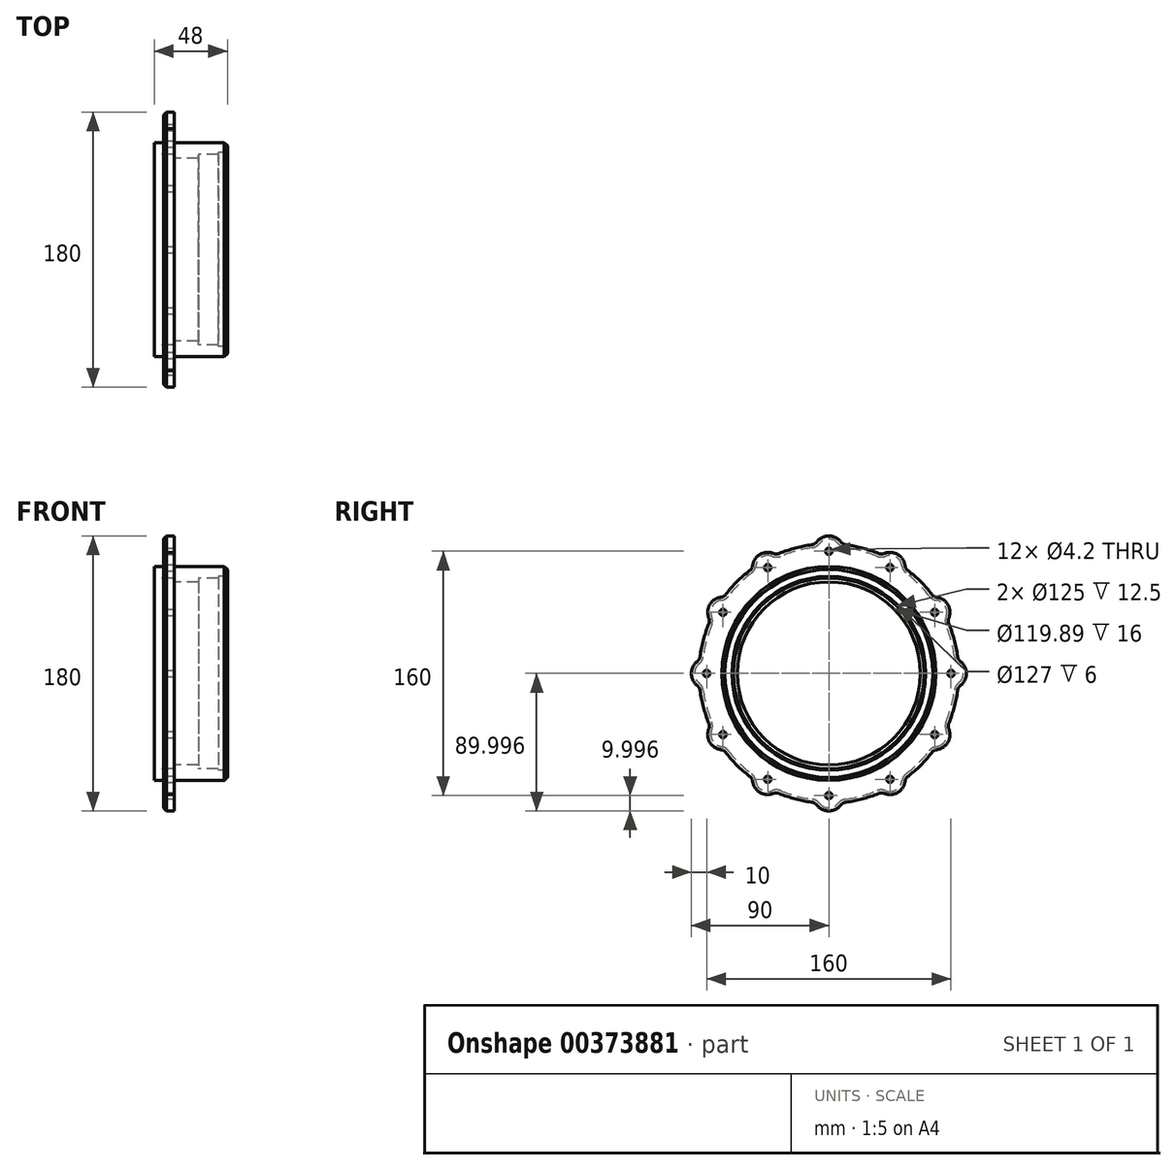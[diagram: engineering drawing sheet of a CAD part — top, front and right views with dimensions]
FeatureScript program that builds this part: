
annotation { "Feature Type Name" : "Feature", "Feature Type Description" : "" }
export const myFeature = defineFeature(function(context is Context, id is Id, definition is map)
    precondition{}
    {
        {
            var Q0;
            Q0=qCreatedBy(makeId("Front.planeOp"),FACE);
            var sketch = newSketch(context, id + "F0", { "sketchPlane" : qUnion([Q0])});
            skLineSegment(sketch, "E0", {"start": v(-16.87, 26.2) * mm, "end": v(-9.87, 26.2) * mm});
            skLineSegment(sketch, "E1", {"start": v(-9.87, 26.2) * mm, "end": v(-9.87, 6.2) * mm});
            skLineSegment(sketch, "E2", {"start": v(-16.87, 26.2) * mm, "end": v(-16.87, 6.2) * mm});
            skLineSegment(sketch, "E3", {"start": v(-16.87, 6.2) * mm, "end": v(-22.87, 6.2) * mm});
            skLineSegment(sketch, "E4", {"start": v(-22.87, 6.2) * mm, "end": v(-22.87, -1.3) * mm});
            skLineSegment(sketch, "E5", {"start": v(-22.87, -1.3) * mm, "end": v(-9.87, -1.3) * mm});
            skLineSegment(sketch, "E6", {"start": v(-9.87, -1.3) * mm, "end": v(-9.87, -3.85) * mm});
            skLineSegment(sketch, "E7", {"start": v(-9.87, -3.85) * mm, "end": v(6.13, -3.85) * mm});
            skLineSegment(sketch, "E8", {"start": v(6.13, -3.85) * mm, "end": v(6.13, -1.3) * mm});
            skLineSegment(sketch, "E9", {"start": v(6.13, -1.3) * mm, "end": v(19.13, -1.3) * mm});
            skLineSegment(sketch, "E10", {"start": v(-16.87, -63.8) * mm, "end": v(53.32, -63.8) * mm, "construction": true});
            skLineSegment(sketch, "E11", {"start": v(19.13, -1.3) * mm, "end": v(19.13, -0.3) * mm});
            skLineSegment(sketch, "E12", {"start": v(19.13, -0.3) * mm, "end": v(25.13, -0.3) * mm});
            skLineSegment(sketch, "E13", {"start": v(-9.87, 6.2) * mm, "end": v(25.13, 6.2) * mm});
            skLineSegment(sketch, "E14", {"start": v(25.13, 6.2) * mm, "end": v(25.13, -0.3) * mm});
            skSolve(sketch);
        }
        {
            var Q0;
            Q0 = qSketchRegion(id + "F0", true);
            var Q1;
            Q1=sQuery(id+"F0.wireOp",EDGE,"E10");
            revolve(context, id + "F1", {"entities" : qUnion([Q0]), "axis" : qUnion([Q1]), "revolveType" : RevolveType.FULL});
        }
        {
            var Q0;
            Q0=makeQuery(id+"F1.opRevolve","SWEPT_FACE",FACE,{"disambiguationData":[OSD([sQuery(id+"F0.wireOp",EDGE,"E2")])]});
            var sketch = newSketch(context, id + "F2", { "sketchPlane" : qUnion([Q0])});
            skLineSegment(sketch, "E15", {"start": v(0, -63.8) * mm, "end": v(0, 16.2) * mm, "construction": true});
            skPoint(sketch, "E16", {"position": v(0, 16.2) * mm});
            skPoint(sketch, "E17.1.0", {"position": v(-40, 5.49) * mm});
            skPoint(sketch, "E17.2.0", {"position": v(-69.28, -23.8) * mm});
            skPoint(sketch, "E17.3.0", {"position": v(-80, -63.8) * mm});
            skPoint(sketch, "E17.4.0", {"position": v(-69.28, -103.8) * mm});
            skPoint(sketch, "E17.5.0", {"position": v(-40, -133.08) * mm});
            skPoint(sketch, "E17.6.0", {"position": v(0, -143.8) * mm});
            skPoint(sketch, "E17.7.0", {"position": v(40, -133.08) * mm});
            skPoint(sketch, "E17.8.0", {"position": v(69.28, -103.8) * mm});
            skPoint(sketch, "E17.9.0", {"position": v(80, -63.8) * mm});
            skPoint(sketch, "E17.10.0", {"position": v(69.28, -23.8) * mm});
            skPoint(sketch, "E17.11.0", {"position": v(40, 5.49) * mm});
            skPoint(sketch, "E17.center", {"position": v(0, -63.8) * mm});
            skSolve(sketch);
        }
        {
            var Q0;
            Q0=sQuery(id+"F2.wireOp",VERTEX,"E16");
            var Q1;
            Q1=sQuery(id+"F2.wireOp",VERTEX,"E17.11.0");
            var Q2;
            Q2=sQuery(id+"F2.wireOp",VERTEX,"E17.10.0");
            var Q3;
            Q3=sQuery(id+"F2.wireOp",VERTEX,"E17.9.0");
            var Q4;
            Q4=sQuery(id+"F2.wireOp",VERTEX,"E17.8.0");
            var Q5;
            Q5=sQuery(id+"F2.wireOp",VERTEX,"E17.7.0");
            var Q6;
            Q6=sQuery(id+"F2.wireOp",VERTEX,"E17.6.0");
            var Q7;
            Q7=sQuery(id+"F2.wireOp",VERTEX,"E17.5.0");
            var Q8;
            Q8=sQuery(id+"F2.wireOp",VERTEX,"E17.4.0");
            var Q9;
            Q9=sQuery(id+"F2.wireOp",VERTEX,"E17.3.0");
            var Q10;
            Q10=sQuery(id+"F2.wireOp",VERTEX,"E17.2.0");
            var Q11;
            Q11=sQuery(id+"F2.wireOp",VERTEX,"E17.1.0");
            var Q12;
            Q12=makeQuery(id+"F1.opRevolve","SWEPT_BODY",BODY,{"disambiguationData":[OSD([sQuery(id+"F0.wireOp",EDGE,"E0"),sQuery(id+"F0.wireOp",EDGE,"E1"),sQuery(id+"F0.wireOp",EDGE,"E2"),sQuery(id+"F0.wireOp",EDGE,"E3"),sQuery(id+"F0.wireOp",EDGE,"E4"),sQuery(id+"F0.wireOp",EDGE,"E5"),sQuery(id+"F0.wireOp",EDGE,"E6"),sQuery(id+"F0.wireOp",EDGE,"E7"),sQuery(id+"F0.wireOp",EDGE,"E8"),sQuery(id+"F0.wireOp",EDGE,"E9"),sQuery(id+"F0.wireOp",EDGE,"E11"),sQuery(id+"F0.wireOp",EDGE,"E12"),sQuery(id+"F0.wireOp",EDGE,"E13"),sQuery(id+"F0.wireOp",EDGE,"E14")])]});
            hole(context, id + "F3", {"style" : HoleStyle.SIMPLE, "endStyle" : HoleEndStyle.THROUGH, "standardTappedOrClearance" : lookupTablePath({ "standard" : "ISO", "engagement" : "75%", "pitch" : "0.8 mm", "size" : "M5", "type" : "Tapped" }), "standardBlindInLast" : lookupTablePath({ "standard" : "ISO", "engagement" : "75%", "pitch" : "0.8 mm", "size" : "M5", "type" : "Tapped" }), "holeDiameter" : 4.2 * mm, "showTappedDepth" : true, "isTappedThrough" : true, "tappedDepth" : 16.82 * mm, "tapClearance" : 3, "locations" : qUnion([Q0, Q1, Q2, Q3, Q4, Q5, Q6, Q7, Q8, Q9, Q10, Q11]), "scope" : qUnion([Q12]), "majorDiameter" : 5 * mm, "startStyle" : HoleStartStyle.SKETCH});
        }
        {
            var Q0;
            Q0=makeQuery(id+"F1.opRevolve","SWEPT_FACE",FACE,{"disambiguationData":[OSD([sQuery(id+"F0.wireOp",EDGE,"E1")])]});
            var sketch = newSketch(context, id + "F4", { "sketchPlane" : qUnion([Q0])});
            skArc(sketch, "E18", {"start": v(45, 14.15) * mm, "mid": v(40.7, 15.46) * mm, "end": v(36.24, 14.75) * mm});
            skArc(sketch, "E19", {"start": v(7.89, 22.35) * mm, "mid": v(4.39, 25.2) * mm, "end": v(0, 26.2) * mm});
            skArc(sketch, "E20", {"start": v(32.45, 14.77) * mm, "mid": v(22, 18.3) * mm, "end": v(11.18, 20.47) * mm});
            skLineSegment(sketch, "E21", {"start": v(0, -63.8) * mm, "end": v(0, 34.34) * mm, "construction": true});
            skLineSegment(sketch, "E22", {"start": v(0, -63.8) * mm, "end": v(49.04, 21.14) * mm, "construction": true});
            skPoint(sketch, "E23.visualSharp", {"position": v(8.91, 20.74) * mm});
            skArc(sketch, "E23.filletArc", {"start": v(7.89, 22.35) * mm, "mid": v(9.35, 21.09) * mm, "end": v(11.18, 20.47) * mm});
            skPoint(sketch, "E24.visualSharp", {"position": v(34.55, 13.87) * mm});
            skArc(sketch, "E24.filletArc", {"start": v(32.45, 14.77) * mm, "mid": v(34.35, 14.39) * mm, "end": v(36.24, 14.75) * mm});
            skPoint(sketch, "E25.1.0", {"position": v(-34.55, 13.87) * mm});
            skArc(sketch, "E25.1.1", {"start": v(-11.18, 20.47) * mm, "mid": v(-22, 18.3) * mm, "end": v(-32.45, 14.77) * mm});
            skArc(sketch, "E25.1.2", {"start": v(-36.24, 14.75) * mm, "mid": v(-40.7, 15.46) * mm, "end": v(-45, 14.15) * mm});
            skPoint(sketch, "E25.1.3", {"position": v(-8.91, 20.74) * mm});
            skArc(sketch, "E25.1.4", {"start": v(0, 26.2) * mm, "mid": v(-4.39, 25.2) * mm, "end": v(-7.89, 22.35) * mm});
            skArc(sketch, "E25.1.5", {"start": v(-11.18, 20.47) * mm, "mid": v(-9.35, 21.09) * mm, "end": v(-7.89, 22.35) * mm});
            skArc(sketch, "E25.1.6", {"start": v(-36.24, 14.75) * mm, "mid": v(-34.35, 14.39) * mm, "end": v(-32.45, 14.77) * mm});
            skPoint(sketch, "E25.2.0", {"position": v(-68.75, -13.8) * mm});
            skArc(sketch, "E25.2.1", {"start": v(-51.8, 3.6) * mm, "mid": v(-60.1, -3.7) * mm, "end": v(-67.39, -11.98) * mm});
            skArc(sketch, "E25.2.2", {"start": v(-70.66, -13.89) * mm, "mid": v(-74.87, -15.5) * mm, "end": v(-77.94, -18.8) * mm});
            skPoint(sketch, "E25.2.3", {"position": v(-49.99, 4.95) * mm});
            skArc(sketch, "E25.2.4", {"start": v(-45, 14.15) * mm, "mid": v(-48.3, 11.07) * mm, "end": v(-49.9, 6.87) * mm});
            skArc(sketch, "E25.2.5", {"start": v(-51.8, 3.6) * mm, "mid": v(-50.53, 5.04) * mm, "end": v(-49.9, 6.87) * mm});
            skArc(sketch, "E25.2.6", {"start": v(-70.66, -13.89) * mm, "mid": v(-68.84, -13.26) * mm, "end": v(-67.39, -11.98) * mm});
            skPoint(sketch, "E25.3.0", {"position": v(-84.53, -54.88) * mm});
            skArc(sketch, "E25.3.1", {"start": v(-78.56, -31.34) * mm, "mid": v(-82.1, -41.8) * mm, "end": v(-84.26, -52.62) * mm});
            skArc(sketch, "E25.3.2", {"start": v(-86.15, -55.9) * mm, "mid": v(-88.98, -59.4) * mm, "end": v(-90, -63.8) * mm});
            skPoint(sketch, "E25.3.3", {"position": v(-77.66, -29.25) * mm});
            skArc(sketch, "E25.3.4", {"start": v(-77.94, -18.8) * mm, "mid": v(-79.26, -23.1) * mm, "end": v(-78.55, -27.55) * mm});
            skArc(sketch, "E25.3.5", {"start": v(-78.56, -31.34) * mm, "mid": v(-78.18, -29.45) * mm, "end": v(-78.55, -27.55) * mm});
            skArc(sketch, "E25.3.6", {"start": v(-86.15, -55.9) * mm, "mid": v(-84.88, -54.45) * mm, "end": v(-84.26, -52.62) * mm});
            skPoint(sketch, "E25.4.0", {"position": v(-77.66, -98.34) * mm});
            skArc(sketch, "E25.4.1", {"start": v(-84.26, -74.97) * mm, "mid": v(-82.1, -85.8) * mm, "end": v(-78.56, -96.25) * mm});
            skArc(sketch, "E25.4.2", {"start": v(-78.55, -100.04) * mm, "mid": v(-79.26, -104.48) * mm, "end": v(-77.94, -108.8) * mm});
            skPoint(sketch, "E25.4.3", {"position": v(-84.53, -72.7) * mm});
            skArc(sketch, "E25.4.4", {"start": v(-90, -63.8) * mm, "mid": v(-88.98, -68.18) * mm, "end": v(-86.15, -71.68) * mm});
            skArc(sketch, "E25.4.5", {"start": v(-84.26, -74.97) * mm, "mid": v(-84.88, -73.14) * mm, "end": v(-86.15, -71.68) * mm});
            skArc(sketch, "E25.4.6", {"start": v(-78.55, -100.04) * mm, "mid": v(-78.18, -98.14) * mm, "end": v(-78.56, -96.25) * mm});
            skPoint(sketch, "E25.5.0", {"position": v(-49.99, -132.54) * mm});
            skArc(sketch, "E25.5.1", {"start": v(-67.39, -115.6) * mm, "mid": v(-60.1, -123.9) * mm, "end": v(-51.8, -131.18) * mm});
            skArc(sketch, "E25.5.2", {"start": v(-49.9, -134.45) * mm, "mid": v(-48.3, -138.66) * mm, "end": v(-45, -141.74) * mm});
            skPoint(sketch, "E25.5.3", {"position": v(-68.75, -113.78) * mm});
            skArc(sketch, "E25.5.4", {"start": v(-77.94, -108.8) * mm, "mid": v(-74.87, -112.09) * mm, "end": v(-70.66, -113.7) * mm});
            skArc(sketch, "E25.5.5", {"start": v(-67.39, -115.6) * mm, "mid": v(-68.84, -114.33) * mm, "end": v(-70.66, -113.7) * mm});
            skArc(sketch, "E25.5.6", {"start": v(-49.9, -134.45) * mm, "mid": v(-50.53, -132.63) * mm, "end": v(-51.8, -131.18) * mm});
            skPoint(sketch, "E25.6.0", {"position": v(-8.91, -148.33) * mm});
            skArc(sketch, "E25.6.1", {"start": v(-32.45, -142.36) * mm, "mid": v(-22, -145.9) * mm, "end": v(-11.18, -148.06) * mm});
            skArc(sketch, "E25.6.2", {"start": v(-7.89, -149.94) * mm, "mid": v(-4.39, -152.78) * mm, "end": v(0, -153.8) * mm});
            skPoint(sketch, "E25.6.3", {"position": v(-34.55, -141.46) * mm});
            skArc(sketch, "E25.6.4", {"start": v(-45, -141.74) * mm, "mid": v(-40.7, -143.05) * mm, "end": v(-36.24, -142.34) * mm});
            skArc(sketch, "E25.6.5", {"start": v(-32.45, -142.36) * mm, "mid": v(-34.35, -141.98) * mm, "end": v(-36.24, -142.34) * mm});
            skArc(sketch, "E25.6.6", {"start": v(-7.89, -149.94) * mm, "mid": v(-9.35, -148.67) * mm, "end": v(-11.18, -148.06) * mm});
            skPoint(sketch, "E25.7.0", {"position": v(34.55, -141.46) * mm});
            skArc(sketch, "E25.7.1", {"start": v(11.18, -148.06) * mm, "mid": v(22, -145.9) * mm, "end": v(32.45, -142.36) * mm});
            skArc(sketch, "E25.7.2", {"start": v(36.24, -142.34) * mm, "mid": v(40.7, -143.05) * mm, "end": v(45, -141.74) * mm});
            skPoint(sketch, "E25.7.3", {"position": v(8.91, -148.33) * mm});
            skArc(sketch, "E25.7.4", {"start": v(0, -153.8) * mm, "mid": v(4.39, -152.78) * mm, "end": v(7.89, -149.94) * mm});
            skArc(sketch, "E25.7.5", {"start": v(11.18, -148.06) * mm, "mid": v(9.35, -148.67) * mm, "end": v(7.89, -149.94) * mm});
            skArc(sketch, "E25.7.6", {"start": v(36.24, -142.34) * mm, "mid": v(34.35, -141.98) * mm, "end": v(32.45, -142.36) * mm});
            skPoint(sketch, "E25.8.0", {"position": v(68.75, -113.78) * mm});
            skArc(sketch, "E25.8.1", {"start": v(51.8, -131.18) * mm, "mid": v(60.1, -123.9) * mm, "end": v(67.39, -115.6) * mm});
            skArc(sketch, "E25.8.2", {"start": v(70.66, -113.7) * mm, "mid": v(74.87, -112.09) * mm, "end": v(77.94, -108.8) * mm});
            skPoint(sketch, "E25.8.3", {"position": v(49.99, -132.54) * mm});
            skArc(sketch, "E25.8.4", {"start": v(45, -141.74) * mm, "mid": v(48.3, -138.66) * mm, "end": v(49.9, -134.45) * mm});
            skArc(sketch, "E25.8.5", {"start": v(51.8, -131.18) * mm, "mid": v(50.53, -132.63) * mm, "end": v(49.9, -134.45) * mm});
            skArc(sketch, "E25.8.6", {"start": v(70.66, -113.7) * mm, "mid": v(68.84, -114.33) * mm, "end": v(67.39, -115.6) * mm});
            skPoint(sketch, "E25.9.0", {"position": v(84.53, -72.7) * mm});
            skArc(sketch, "E25.9.1", {"start": v(78.56, -96.25) * mm, "mid": v(82.1, -85.8) * mm, "end": v(84.26, -74.97) * mm});
            skArc(sketch, "E25.9.2", {"start": v(86.15, -71.68) * mm, "mid": v(88.98, -68.18) * mm, "end": v(90, -63.8) * mm});
            skPoint(sketch, "E25.9.3", {"position": v(77.66, -98.34) * mm});
            skArc(sketch, "E25.9.4", {"start": v(77.94, -108.8) * mm, "mid": v(79.26, -104.48) * mm, "end": v(78.55, -100.04) * mm});
            skArc(sketch, "E25.9.5", {"start": v(78.56, -96.25) * mm, "mid": v(78.18, -98.14) * mm, "end": v(78.55, -100.04) * mm});
            skArc(sketch, "E25.9.6", {"start": v(86.15, -71.68) * mm, "mid": v(84.88, -73.14) * mm, "end": v(84.26, -74.97) * mm});
            skPoint(sketch, "E25.10.0", {"position": v(77.66, -29.25) * mm});
            skArc(sketch, "E25.10.1", {"start": v(84.26, -52.62) * mm, "mid": v(82.1, -41.8) * mm, "end": v(78.56, -31.34) * mm});
            skArc(sketch, "E25.10.2", {"start": v(78.55, -27.55) * mm, "mid": v(79.26, -23.1) * mm, "end": v(77.94, -18.8) * mm});
            skPoint(sketch, "E25.10.3", {"position": v(84.53, -54.88) * mm});
            skArc(sketch, "E25.10.4", {"start": v(90, -63.8) * mm, "mid": v(88.98, -59.4) * mm, "end": v(86.15, -55.9) * mm});
            skArc(sketch, "E25.10.5", {"start": v(84.26, -52.62) * mm, "mid": v(84.88, -54.45) * mm, "end": v(86.15, -55.9) * mm});
            skArc(sketch, "E25.10.6", {"start": v(78.55, -27.55) * mm, "mid": v(78.18, -29.45) * mm, "end": v(78.56, -31.34) * mm});
            skPoint(sketch, "E25.11.0", {"position": v(49.99, 4.95) * mm});
            skArc(sketch, "E25.11.1", {"start": v(67.39, -11.98) * mm, "mid": v(60.1, -3.7) * mm, "end": v(51.8, 3.6) * mm});
            skArc(sketch, "E25.11.2", {"start": v(49.9, 6.87) * mm, "mid": v(48.3, 11.07) * mm, "end": v(45, 14.15) * mm});
            skPoint(sketch, "E25.11.3", {"position": v(68.75, -13.8) * mm});
            skArc(sketch, "E25.11.4", {"start": v(77.94, -18.8) * mm, "mid": v(74.87, -15.5) * mm, "end": v(70.66, -13.89) * mm});
            skArc(sketch, "E25.11.5", {"start": v(67.39, -11.98) * mm, "mid": v(68.84, -13.26) * mm, "end": v(70.66, -13.89) * mm});
            skArc(sketch, "E25.11.6", {"start": v(49.9, 6.87) * mm, "mid": v(50.53, 5.04) * mm, "end": v(51.8, 3.6) * mm});
            skCircle(sketch, "E26", {"center": v(0, -63.8) * mm, "radius": 105.65 * mm});
            skSolve(sketch);
        }
        {
            var Q0;
            Q0 = qSketchRegion(id + "F4", true);
            extrude(context, id + "F5", {"entities" : qUnion([Q0]), "operationType" : NewBodyOperationType.REMOVE, "endBound" : BoundingType.THROUGH_ALL, "oppositeDirection" : true, "depth" : 25 * mm, "offsetDistance" : 25 * mm});
        }
        {
            var Q0;
            Q0=makeQuery(id+"F1.opRevolve","SWEPT_EDGE",EDGE,{"disambiguationData":[OSD([sQuery(id+"F0.wireOp",EDGE,"E13"),sQuery(id+"F0.wireOp",EDGE,"E14")])]});
            var Q1;
            Q1=makeQuery(id+"F1.opRevolve","SWEPT_EDGE",EDGE,{"disambiguationData":[OSD([sQuery(id+"F0.wireOp",EDGE,"E0"),sQuery(id+"F0.wireOp",EDGE,"E2")])]});
            chamfer(context, id + "F6", {"entities" : qUnion([Q0, Q1]), "width" : 2 * mm, "tangentPropagation" : true});
        }
        {
            var Q0;
            Q0=makeQuery(id+"F5.boolean.opBoolean","INTERSECT",EDGE,{"derivedFrom":[makeQuery(id+"F1.opRevolve","SWEPT_FACE",FACE,{"disambiguationData":[OSD([sQuery(id+"F0.wireOp",EDGE,"E2")])]}),makeQuery(id+"F5.opExtrude","SWEPT_FACE",FACE,{"disambiguationData":[OSD([sQuery(id+"F4.wireOp",EDGE,"E20")])]})]});
            chamfer(context, id + "F7", {"entities" : qUnion([Q0]), "width" : 2 * mm, "tangentPropagation" : true});
        }
        {
            var Q0;
            Q0=makeQuery(id+"F1.opRevolve","SWEPT_EDGE",EDGE,{"disambiguationData":[OSD([sQuery(id+"F0.wireOp",EDGE,"E8"),sQuery(id+"F0.wireOp",EDGE,"E9")])]});
            fillet(context, id + "F8", {"entities" : qUnion([Q0]), "radius" : .5 * mm, "tangentPropagation" : true, "allowEdgeOverflow" : false});
        }
        {
            var Q0;
            Q0=makeQuery(id+"F1.opRevolve","SWEPT_EDGE",EDGE,{"disambiguationData":[OSD([sQuery(id+"F0.wireOp",EDGE,"E5"),sQuery(id+"F0.wireOp",EDGE,"E6")])]});
            fillet(context, id + "F9", {"entities" : qUnion([Q0]), "radius" : .5 * mm, "tangentPropagation" : true, "allowEdgeOverflow" : false});
        }
        {
            var Q0;
            Q0=makeQuery(id+"F1.opRevolve","SWEPT_EDGE",EDGE,{"disambiguationData":[OSD([sQuery(id+"F0.wireOp",EDGE,"E2"),sQuery(id+"F0.wireOp",EDGE,"E3")])]});
            var Q1;
            Q1=makeQuery(id+"F1.opRevolve","SWEPT_EDGE",EDGE,{"disambiguationData":[OSD([sQuery(id+"F0.wireOp",EDGE,"E1"),sQuery(id+"F0.wireOp",EDGE,"E13")])]});
            fillet(context, id + "F10", {"entities" : qUnion([Q0, Q1]), "radius" : .5 * mm, "tangentPropagation" : true, "allowEdgeOverflow" : false});
        }
    });
